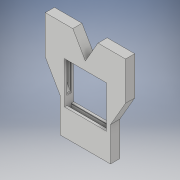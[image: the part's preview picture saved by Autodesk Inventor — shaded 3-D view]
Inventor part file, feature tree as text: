
AUTODESK INVENTOR PART (.ipt)
format: ipt  version: 2017 (Build 210142000, 142)  size: 305,664 bytes
history: native  units: in
note: dims shown in document units (in); Inventor stores cm internally (conversion verified against a paired STEP export)
features: extrude x7, sketch x7, other x3
ambient origin geometry x8: Origin, YZ Plane, XZ Plane, XY Plane, X Axis, Y Axis, Z Axis, Center Point
bodies: Body1 (feature_tree)
feature tree (17):
  other  "rame of door"
  extrude  "frame"  Depth=100.0in
  other  "middle of part"
  extrude  "door slot bottom"  Depth=10.0in
  extrude  "top left and right slots"  Depth=10.0in
  extrude  "slots for hiding bars"  Depth=22.0in
  extrude  "door recieves"  Depth=10.0in TaperAngle=0.0deg
  extrude  "front hide door"  Depth=2.0in
  extrude  "gap for door pieces"  Depth=1.0in
  other  "mate for door pieces"
  sketch  "Sketch1"  dims[d0=100.0in d1=100.0in]
  sketch  "Sketch7"  dims[d3=10.0in d4=10.0in]
  sketch  "Sketch8"  dims[d5=10.0in d6=10.0in]
  sketch  "Sketch12"  dims[d7=22.0in d8=0.0in d118=0.7071in d178=0.8316in]
  sketch  "Sketch13"  dims[d459=10.0in d460=0.0in d865=10.0in d866=0.0in]
  sketch  "Sketch14"  dims[d878=60.0deg d889=2.0in]
  sketch  "Sketch15"  dims[d890=1.0in d891=1.0in d893=1.0in d894=1.0in d895=1.0in d898=20.0in d899=0.0in d901=2.0in d902=78.8675in d903=51.0in d907=10.0in d916=10.0in d917=10.0in d919=10.0in d920=10.0in d921=10.0in d922=22.0in d923=0.0in d926=25.7957in d927=52.0in d928=21.0in d929=0.0in d930=10.0in d931=0.0in d932=50.0in]
